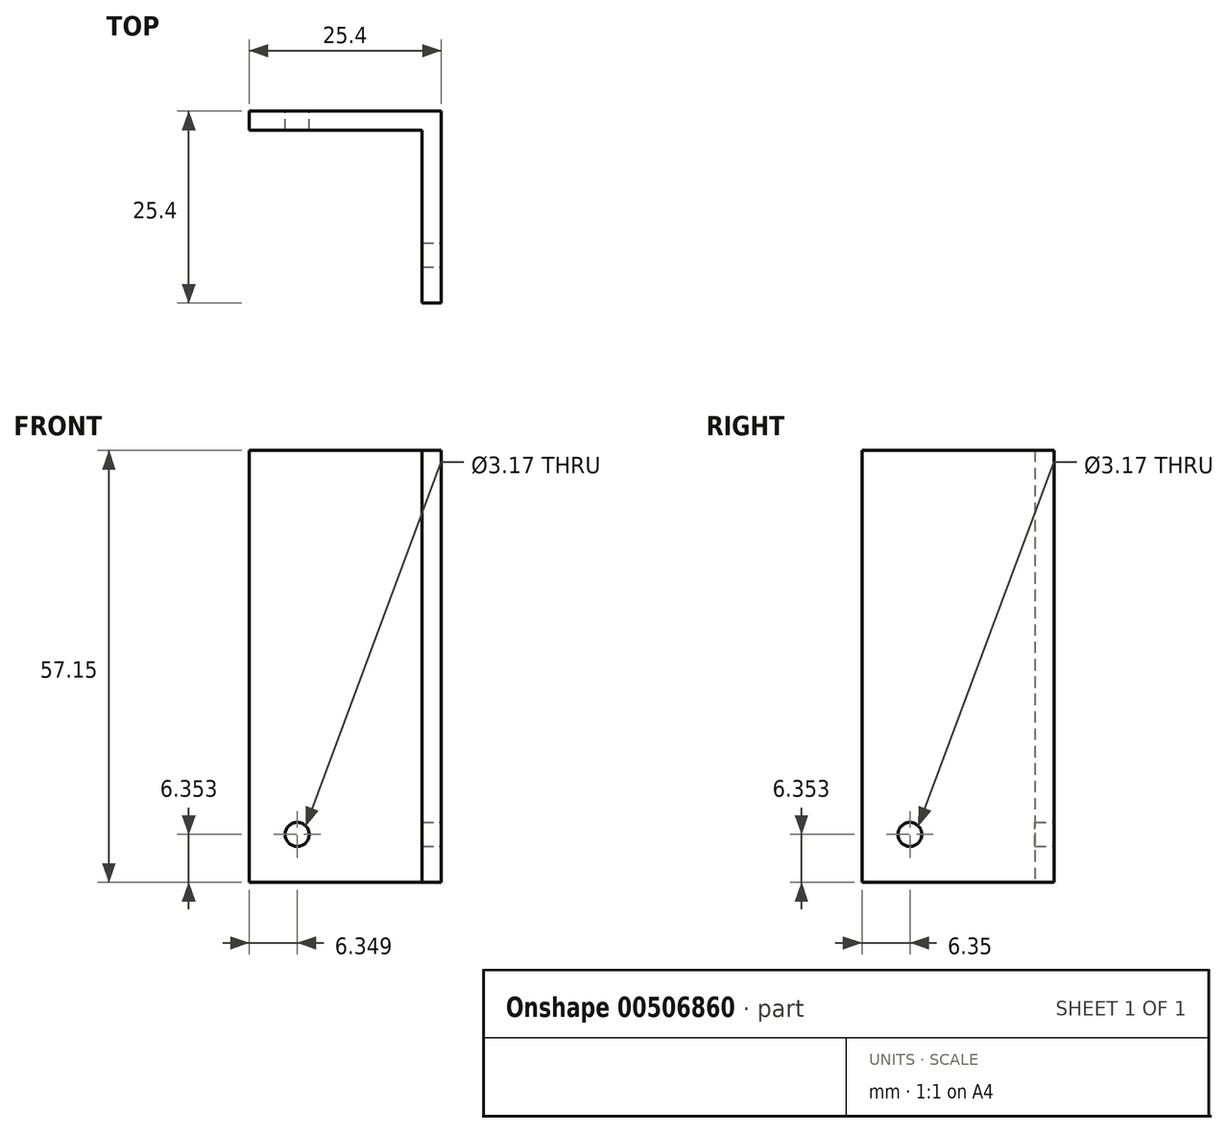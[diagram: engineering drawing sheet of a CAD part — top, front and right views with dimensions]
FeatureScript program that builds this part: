
annotation { "Feature Type Name" : "Feature", "Feature Type Description" : "" }
export const myFeature = defineFeature(function(context is Context, id is Id, definition is map)
    precondition{}
    {
        {
            var Q0;
            Q0=qCreatedBy(makeId("Front.planeOp"),FACE);
            var sketch = newSketch(context, id + "F0", { "sketchPlane" : qUnion([Q0])});
            skLineSegment(sketch, "E0.bottom", {"start": v(14.44, 27.28) * mm, "end": v(39.84, 27.28) * mm});
            skLineSegment(sketch, "E0.top", {"start": v(14.44, -29.87) * mm, "end": v(39.84, -29.87) * mm});
            skLineSegment(sketch, "E0.left", {"start": v(14.44, 27.28) * mm, "end": v(14.44, -29.87) * mm});
            skLineSegment(sketch, "E0.right", {"start": v(39.84, 27.28) * mm, "end": v(39.84, -29.87) * mm});
            skSolve(sketch);
        }
        {
            var Q0;
            Q0=makeQuery(id+"F0.imprint","IMPRINT",FACE,{"disambiguationData":[TD([[makeQuery(id+"F0.imprint","IMPRINT",EDGE,{"derivedFrom":sQuery(id+"F0.wireOp",EDGE,"E0.bottom")}),-1.0]])]});
            extrude(context, id + "F1", {"entities" : qUnion([Q0]), "depth" : 25.4 * mm, "offsetDistance" : 25.4 * mm});
        }
        {
            var Q0;
            Q0=makeQuery(id+"F1.opExtrude","SWEPT_FACE",FACE,{"disambiguationData":[OSD([sQuery(id+"F0.wireOp",EDGE,"E0.bottom")])]});
            var Q1;
            Q1=makeQuery(id+"F1.opExtrude","CAP_FACE",FACE,{"disambiguationData":[OSD([sQuery(id+"F0.wireOp",EDGE,"E0.bottom"),sQuery(id+"F0.wireOp",EDGE,"E0.top"),sQuery(id+"F0.wireOp",EDGE,"E0.left"),sQuery(id+"F0.wireOp",EDGE,"E0.right")])],"isStart":false});
            var Q2;
            Q2=makeQuery(id+"F1.opExtrude","SWEPT_FACE",FACE,{"disambiguationData":[OSD([sQuery(id+"F0.wireOp",EDGE,"E0.left")])]});
            var Q3;
            Q3=makeQuery(id+"F1.opExtrude","SWEPT_FACE",FACE,{"disambiguationData":[OSD([sQuery(id+"F0.wireOp",EDGE,"E0.top")])]});
            shell(context, id + "F2", {"entities" : qUnion([Q0, Q1, Q2, Q3]), "thickness" : 2.54 * mm});
        }
        {
            var Q0;
            Q0=makeQuery(id+"F1.opExtrude","SWEPT_FACE",FACE,{"disambiguationData":[OSD([sQuery(id+"F0.wireOp",EDGE,"E0.right")])]});
            var sketch = newSketch(context, id + "F3", { "sketchPlane" : qUnion([Q0])});
            skPoint(sketch, "E1", {"position": v(-19.05, -23.52) * mm});
            skPoint(sketch, "E2", {"position": v(-19.05, -29.87) * mm});
            skPoint(sketch, "E3", {"position": v(-25.4, -23.31) * mm});
            skSolve(sketch);
        }
        {
            var Q0;
            Q0=sQuery(id+"F3.wireOp",VERTEX,"E1");
            var Q1;
            Q1=makeQuery(id+"F1.opExtrude","SWEPT_BODY",BODY,{"disambiguationData":[OSD([sQuery(id+"F0.wireOp",EDGE,"E0.bottom"),sQuery(id+"F0.wireOp",EDGE,"E0.top"),sQuery(id+"F0.wireOp",EDGE,"E0.left"),sQuery(id+"F0.wireOp",EDGE,"E0.right")])]});
            hole(context, id + "F4", {"style" : HoleStyle.SIMPLE, "endStyle" : HoleEndStyle.THROUGH, "holeDiameter" : 3.17 * mm, "majorDiameter" : 6.35 * mm, "isTappedThrough" : true, "tappedDepth" : 12.7 * mm, "tapClearance" : 3, "locations" : qUnion([Q0]), "scope" : qUnion([Q1])});
        }
        {
            var Q0;
            Q0=makeQuery(id+"F1.opExtrude","CAP_FACE",FACE,{"disambiguationData":[OSD([sQuery(id+"F0.wireOp",EDGE,"E0.bottom"),sQuery(id+"F0.wireOp",EDGE,"E0.top"),sQuery(id+"F0.wireOp",EDGE,"E0.left"),sQuery(id+"F0.wireOp",EDGE,"E0.right")])],"isStart":true});
            var sketch = newSketch(context, id + "F5", { "sketchPlane" : qUnion([Q0])});
            skPoint(sketch, "E4", {"position": v(-20.79, -23.52) * mm});
            skSolve(sketch);
        }
        {
            var Q0;
            Q0=sQuery(id+"F5.wireOp",VERTEX,"E4");
            var Q1;
            Q1=makeQuery(id+"F1.opExtrude","SWEPT_BODY",BODY,{"disambiguationData":[OSD([sQuery(id+"F0.wireOp",EDGE,"E0.bottom"),sQuery(id+"F0.wireOp",EDGE,"E0.top"),sQuery(id+"F0.wireOp",EDGE,"E0.left"),sQuery(id+"F0.wireOp",EDGE,"E0.right")])]});
            hole(context, id + "F6", {"style" : HoleStyle.SIMPLE, "endStyle" : HoleEndStyle.THROUGH, "holeDiameter" : 3.17 * mm, "majorDiameter" : 6.35 * mm, "isTappedThrough" : true, "tappedDepth" : 12.7 * mm, "tapClearance" : 3, "locations" : qUnion([Q0]), "scope" : qUnion([Q1])});
        }
    });
